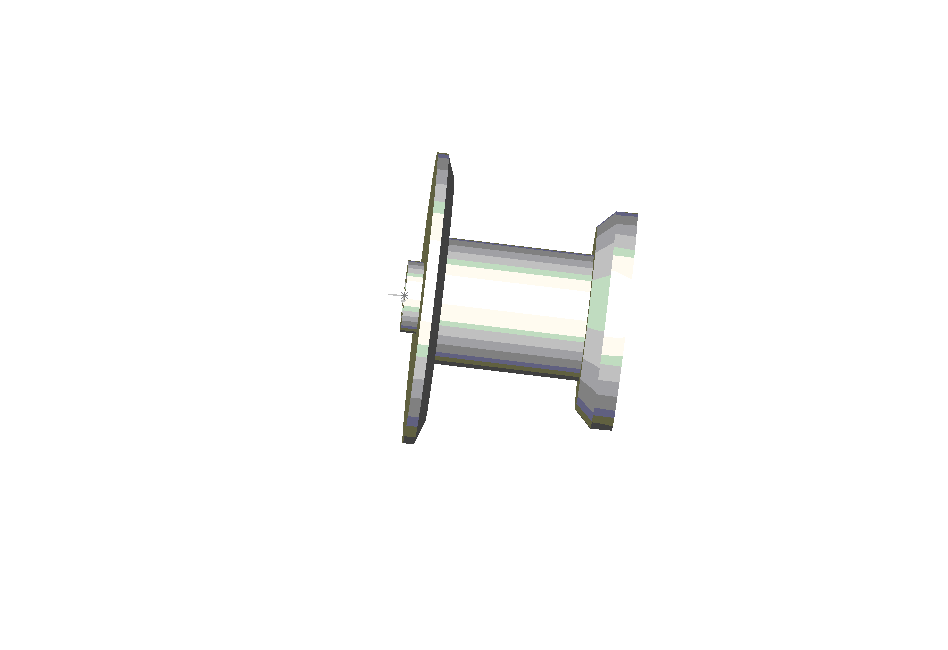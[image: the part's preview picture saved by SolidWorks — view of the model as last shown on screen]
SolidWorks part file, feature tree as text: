
SOLIDWORKS PART (.sldprt)
format: sldprt  version: not decoded by parser v0  size: 67,072 bytes
history: native  units: mm
features: chamfer x3, sketch x1, revolve x1 (+8 scaffold rows collapsed)
feature tree (13):
  scaffold x8  (default folders/planes/origin — collapsed)
  sketch  "Sketch1"  dims[c1.D1=5.5mm c1.D2=3.35mm c1.D3=9.47mm c1.D4=~13.039478mm c2.D4=~118.217356deg c3.D4=1.69mm c3.D5=19.16mm c3.D6=12.65mm c3.D1=9.47mm c3.D3=12.65mm c4.D5=5.5mm c4.D6=3.125mm c4.D7=1.38mm c4.D8=19.15mm c4.D9=2.0mm]
  revolve  "Base-Revolve"  Angle=360deg
  chamfer  "Chamfer1"  Distance=3mm Angle=41deg
  chamfer  "Chamfer2"  Distance=2mm Angle=20deg
  chamfer  "Chamfer3"  Distance=1.5mm Angle=45deg
decode coverage: 5 of 5 modeling features carry decoded parameters
note: ~ marks probable driven/reference dimensions
note: suppression state not decoded; provenance and decode notes live in map.json
